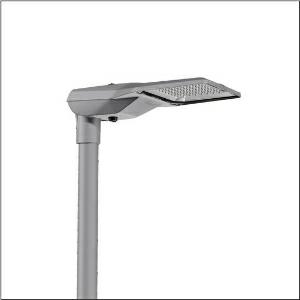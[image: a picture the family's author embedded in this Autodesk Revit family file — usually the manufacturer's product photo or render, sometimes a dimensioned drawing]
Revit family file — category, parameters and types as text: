
# Revit family: streetlight_sl_21_midi___st0_8a_5xe3c23t08nb_0a9c
name_source: partatom
category: Lighting Fixtures
units: mm (PartAtom-declared; Revit-internal decimal feet)

## family parameters
Cut with Voids When Loaded = No
Host = Face
Light Source = No
Part Type = Normal
Room Calculation Point = No
Round Connector Dimension = Use Diameter
Shared = No

## types (1)
- --- (1 x LED, 18780 lm, 151.2 W, 2200K)
    Apparent Load = 151 VA
    CIE Flux Codes = 41 75 97 100 100
    Color Rendering = 70
    Color Temperature = 2200K
    Default Elevation = 1800 mm
    Description = Streetlight SL 21 midi, mast luminaire, primary light control with lens, of PMMA, primary optical cover: cover, of toughened safety glass, transparent, light distribution: ST0.8a, light emission: direct distribution, primary light characteristic: asymmetric, installation type: side-entry, post-top, LED, High Power LED, rated luminous flux: 18.780lm, luminous efficacy: 124lm/W, light colour: 722, colour temperature: 2200K, control gear: D4i, control: overheat protection, constant luminous flux control, time-dependent luminous flux control, flexible luminous flux parameterisation, pre-setting: logarithmic dimming characteristic, mains connection: 230..240V, AC, 50/60Hz, start of lifetime: 151W, end of service life: 157W, reduction: 70W, luminaire housing, of diecast aluminium, powder-coated, SITECO metallic grey (DB 702S), corrosivity category C5 high according to DIN EN ISO 12944, please order mast flange separately, inclination adjustable: 0°, 5°, 10°, 15°, sealing non-destructively replaceable, multi-level sealing system, length: 644mm, width: 335mm, height: 110mm, mast flange for spigot size: 42mm (side-entry): 5XC10008XM4, 60/48mm (side-entry/post-top): 5XC10108XM2, 76/60mm (side-entry/post-top): 5XC10108XM1, mounting height: 4..8m, Smart Interface below and above, protection rating (complete): IP66, insulation class (complete): insulation class II (safety insulation), certification: CE, ENEC, ENEC+, VDE, impact resistance: IK10, permissible operating ambient temperature for outdoor applications: -40..+50°C, standard-compliant lighting for roads and squares, packaging unit: 1 piece

Light Distribution: ST0.8a
    Height = 111 mm
    Lamp = 1 x LED
    Lamp Light Flux = 18780 lm
    Lamp Power = 151.2 W
    Lamp count = 1
    Length = 644 mm
    Luminous efficacy = 124 lm/W
    Manufacturer = Siteco
    ModVariant = No
    Model = 5XE3C23T08NB
    Number of Poles = 1
    OnlyDefault = Yes
    Power Factor = 1
    Product Name = Streetlight SL 21 midi | ST0.8a
    Product group = mast luminaire | pylon top
    ProductGroupID = 6100
    Protection Class = Protection class II
    Protection Degree = IP 66
    RLX_Detail_Level = 1
    RLX_Emergency_Light_Flux = 0 lm
    RLX_Emergency_Type = 0
    RLX_Emergency_Type_DB = No
    RlxData = <blob elided: 27041 chars, md5=acddb83e>
    Socket = socket
    Standby Power = 0 W
    System Light Flux = 18781 lm
    System Power = 151 W
    Type Comments = factory setting: luminous flux: 100 % | dim-lin: 254 | 802 mA
    Type Image = l_1004304.jpg
    URL = http://relux.com
    VarID = @adj_168159
    Voltage = 0 V
    Weight = 0.00 kg
    Width = 336 mm

## geometry (parser evidence)
native form markers: Blend x4, Sweep x11
no freeform markers — native parametric forms only
